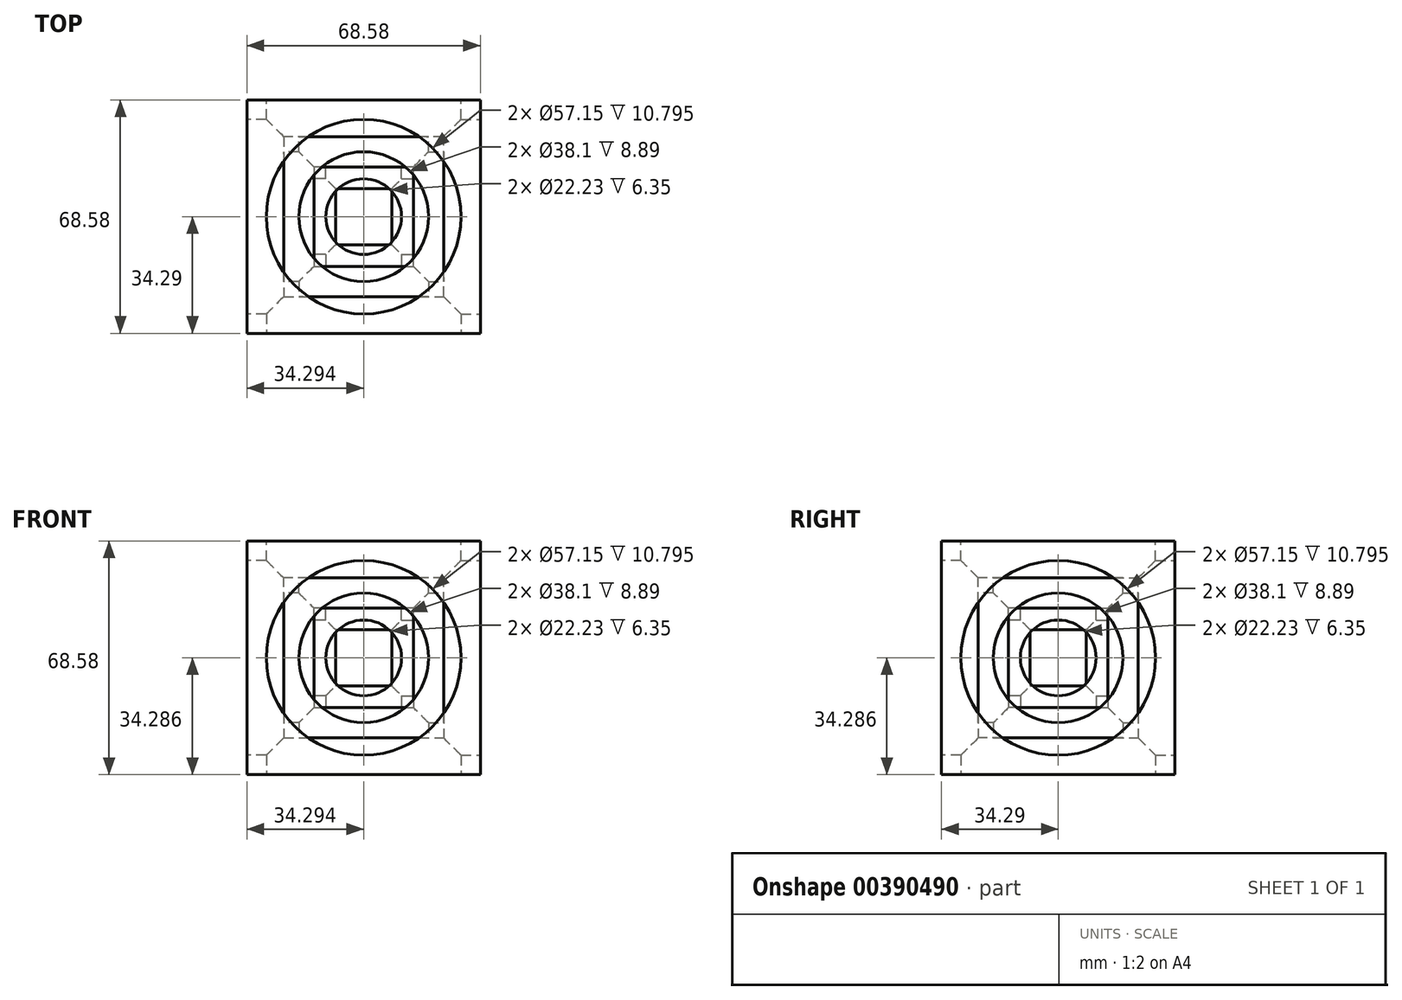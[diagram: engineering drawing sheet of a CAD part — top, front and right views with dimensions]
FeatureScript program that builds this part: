
annotation { "Feature Type Name" : "Feature", "Feature Type Description" : "" }
export const myFeature = defineFeature(function(context is Context, id is Id, definition is map)
    precondition{}
    {
        {
            var Q0;
            Q0=qCreatedBy(makeId("Front.planeOp"),FACE);
            var sketch = newSketch(context, id + "F0", { "sketchPlane" : qUnion([Q0])});
            skLineSegment(sketch, "E0.bottom", {"start": v(-23.47, 31.89) * mm, "end": v(45.11, 31.89) * mm});
            skLineSegment(sketch, "E0.top", {"start": v(-23.47, -36.7) * mm, "end": v(45.11, -36.7) * mm});
            skLineSegment(sketch, "E0.left", {"start": v(-23.47, 31.89) * mm, "end": v(-23.47, -36.7) * mm});
            skLineSegment(sketch, "E0.right", {"start": v(45.11, 31.89) * mm, "end": v(45.11, -36.7) * mm});
            skSolve(sketch);
        }
        {
            var Q0;
            Q0=makeQuery(id+"F0.imprint","IMPRINT",FACE,{"disambiguationData":[TD([[makeQuery(id+"F0.imprint","IMPRINT",EDGE,{"derivedFrom":sQuery(id+"F0.wireOp",EDGE,"E0.bottom")}),-1.0]])]});
            extrude(context, id + "F1", {"entities" : qUnion([Q0]), "depth" : 68.58 * mm});
        }
        {
            var Q0;
            Q0=makeQuery(id+"F1.opExtrude","CAP_FACE",FACE,{"disambiguationData":[OSD([sQuery(id+"F0.wireOp",EDGE,"E0.bottom"),sQuery(id+"F0.wireOp",EDGE,"E0.top"),sQuery(id+"F0.wireOp",EDGE,"E0.left"),sQuery(id+"F0.wireOp",EDGE,"E0.right")])],"isStart":false});
            var sketch = newSketch(context, id + "F2", { "sketchPlane" : qUnion([Q0])});
            skCircle(sketch, "E1", {"center": v(10.82, -2.4) * mm, "radius": 28.58 * mm});
            skPoint(sketch, "E1.centerSnap0", {"position": v(10.82, 31.89) * mm});
            skPoint(sketch, "E1.centerSnap1", {"position": v(-23.47, -2.4) * mm});
            skSolve(sketch);
        }
        {
            var Q0;
            Q0=makeQuery(id+"F2.imprint","IMPRINT",FACE,{"disambiguationData":[TD([[makeQuery(id+"F2.imprint","IMPRINT",EDGE,{"derivedFrom":sQuery(id+"F2.wireOp",EDGE,"E1")}),1.0]])]});
            extrude(context, id + "F3", {"entities" : qUnion([Q0]), "operationType" : NewBodyOperationType.REMOVE, "depth" : -10.8 * mm});
        }
        {
            var Q0;
            Q0=makeQuery(id+"F1.opExtrude","SWEPT_FACE",FACE,{"disambiguationData":[OSD([sQuery(id+"F0.wireOp",EDGE,"E0.right")])]});
            var sketch = newSketch(context, id + "F4", { "sketchPlane" : qUnion([Q0])});
            skCircle(sketch, "E2", {"center": v(-34.3, -2.4) * mm, "radius": 28.58 * mm});
            skPoint(sketch, "E2.centerSnap0", {"position": v(-68.58, -2.4) * mm});
            skPoint(sketch, "E2.centerSnap1", {"position": v(-34.3, 31.89) * mm});
            skSolve(sketch);
        }
        {
            var Q0;
            Q0=makeQuery(id+"F4.imprint","IMPRINT",FACE,{"disambiguationData":[TD([[makeQuery(id+"F4.imprint","IMPRINT",EDGE,{"derivedFrom":sQuery(id+"F4.wireOp",EDGE,"E2")}),1.0]])]});
            extrude(context, id + "F5", {"entities" : qUnion([Q0]), "operationType" : NewBodyOperationType.REMOVE, "oppositeDirection" : true, "depth" : 10.8 * mm});
        }
        {
            var Q0;
            Q0=makeQuery(id+"F1.opExtrude","CAP_FACE",FACE,{"disambiguationData":[OSD([sQuery(id+"F0.wireOp",EDGE,"E0.bottom"),sQuery(id+"F0.wireOp",EDGE,"E0.top"),sQuery(id+"F0.wireOp",EDGE,"E0.left"),sQuery(id+"F0.wireOp",EDGE,"E0.right")])],"isStart":true});
            var sketch = newSketch(context, id + "F6", { "sketchPlane" : qUnion([Q0])});
            skCircle(sketch, "E3", {"center": v(-10.82, -2.4) * mm, "radius": 28.58 * mm});
            skPoint(sketch, "E3.centerSnap0", {"position": v(-45.11, -2.4) * mm});
            skPoint(sketch, "E3.centerSnap1", {"position": v(-10.82, 31.89) * mm});
            skSolve(sketch);
        }
        {
            var Q0;
            Q0=makeQuery(id+"F6.imprint","IMPRINT",FACE,{"disambiguationData":[TD([[makeQuery(id+"F6.imprint","IMPRINT",EDGE,{"derivedFrom":sQuery(id+"F6.wireOp",EDGE,"E3")}),1.0]])]});
            extrude(context, id + "F7", {"entities" : qUnion([Q0]), "operationType" : NewBodyOperationType.REMOVE, "oppositeDirection" : true, "depth" : 10.8 * mm});
        }
        {
            var Q0;
            Q0=makeQuery(id+"F1.opExtrude","SWEPT_FACE",FACE,{"disambiguationData":[OSD([sQuery(id+"F0.wireOp",EDGE,"E0.left")])]});
            var sketch = newSketch(context, id + "F8", { "sketchPlane" : qUnion([Q0])});
            skCircle(sketch, "E4", {"center": v(34.3, -2.4) * mm, "radius": 28.58 * mm});
            skPoint(sketch, "E4.centerSnap0", {"position": v(68.58, -2.4) * mm});
            skPoint(sketch, "E4.centerSnap1", {"position": v(34.3, 31.89) * mm});
            skSolve(sketch);
        }
        {
            var Q0;
            Q0=makeQuery(id+"F8.imprint","IMPRINT",FACE,{"disambiguationData":[TD([[makeQuery(id+"F8.imprint","IMPRINT",EDGE,{"derivedFrom":sQuery(id+"F8.wireOp",EDGE,"E4")}),1.0]])]});
            extrude(context, id + "F9", {"entities" : qUnion([Q0]), "operationType" : NewBodyOperationType.REMOVE, "oppositeDirection" : true, "depth" : 10.8 * mm});
        }
        {
            var Q0;
            Q0=makeQuery(id+"F1.opExtrude","SWEPT_FACE",FACE,{"disambiguationData":[OSD([sQuery(id+"F0.wireOp",EDGE,"E0.bottom")])]});
            var sketch = newSketch(context, id + "F10", { "sketchPlane" : qUnion([Q0])});
            skCircle(sketch, "E5", {"center": v(10.82, -34.3) * mm, "radius": 28.58 * mm});
            skPoint(sketch, "E5.centerSnap0", {"position": v(10.82, -68.58) * mm});
            skPoint(sketch, "E5.centerSnap1", {"position": v(-23.47, -34.3) * mm});
            skSolve(sketch);
        }
        {
            var Q0;
            Q0=makeQuery(id+"F10.imprint","IMPRINT",FACE,{"disambiguationData":[TD([[makeQuery(id+"F10.imprint","IMPRINT",EDGE,{"derivedFrom":sQuery(id+"F10.wireOp",EDGE,"E5")}),1.0]])]});
            extrude(context, id + "F11", {"entities" : qUnion([Q0]), "operationType" : NewBodyOperationType.REMOVE, "oppositeDirection" : true, "depth" : 10.8 * mm});
        }
        {
            var Q0;
            Q0=makeQuery(id+"F1.opExtrude","SWEPT_FACE",FACE,{"disambiguationData":[OSD([sQuery(id+"F0.wireOp",EDGE,"E0.top")])]});
            var sketch = newSketch(context, id + "F12", { "sketchPlane" : qUnion([Q0])});
            skCircle(sketch, "E6", {"center": v(10.82, 34.3) * mm, "radius": 28.58 * mm});
            skPoint(sketch, "E6.centerSnap0", {"position": v(10.82, 68.58) * mm});
            skPoint(sketch, "E6.centerSnap1", {"position": v(-23.47, 34.3) * mm});
            skSolve(sketch);
        }
        {
            var Q0;
            Q0=makeQuery(id+"F12.imprint","IMPRINT",FACE,{"disambiguationData":[TD([[makeQuery(id+"F12.imprint","IMPRINT",EDGE,{"derivedFrom":sQuery(id+"F12.wireOp",EDGE,"E6")}),1.0]])]});
            extrude(context, id + "F13", {"entities" : qUnion([Q0]), "operationType" : NewBodyOperationType.REMOVE, "oppositeDirection" : true, "depth" : 10.8 * mm});
        }
        {
            var Q0;
            Q0=makeQuery(id+"F3.boolean.opBoolean","COPY",FACE,{"derivedFrom":makeQuery(id+"F3.opExtrude","CAP_FACE",FACE,{"disambiguationData":[OSD([sQuery(id+"F2.wireOp",EDGE,"E1")])],"isStart":false})});
            var sketch = newSketch(context, id + "F14", { "sketchPlane" : qUnion([Q0])});
            skPoint(sketch, "E7.centerSnap0", {"position": v(10.82, 21.1) * mm});
            skCircle(sketch, "E8", {"center": v(10.82, -2.4) * mm, "radius": 19.05 * mm});
            skSolve(sketch);
        }
        {
            var Q0;
            Q0=makeQuery(id+"F14.imprint","IMPRINT",FACE,{"disambiguationData":[TD([[makeQuery(id+"F14.imprint","IMPRINT",EDGE,{"derivedFrom":sQuery(id+"F14.wireOp",EDGE,"E8")}),1.0]])]});
            extrude(context, id + "F15", {"entities" : qUnion([Q0]), "operationType" : NewBodyOperationType.REMOVE, "oppositeDirection" : true, "depth" : 8.9 * mm});
        }
        {
            var Q0;
            Q0=makeQuery(id+"F5.boolean.opBoolean","COPY",FACE,{"derivedFrom":makeQuery(id+"F5.opExtrude","CAP_FACE",FACE,{"disambiguationData":[OSD([sQuery(id+"F4.wireOp",EDGE,"E2")])],"isStart":false})});
            var sketch = newSketch(context, id + "F16", { "sketchPlane" : qUnion([Q0])});
            skCircle(sketch, "E9", {"center": v(-34.3, -2.4) * mm, "radius": 19.05 * mm});
            skSolve(sketch);
        }
        {
            var Q0;
            Q0=makeQuery(id+"F16.imprint","IMPRINT",FACE,{"disambiguationData":[TD([[makeQuery(id+"F16.imprint","IMPRINT",EDGE,{"derivedFrom":sQuery(id+"F16.wireOp",EDGE,"E9")}),1.0]])]});
            extrude(context, id + "F17", {"entities" : qUnion([Q0]), "operationType" : NewBodyOperationType.REMOVE, "oppositeDirection" : true, "depth" : 8.9 * mm});
        }
        {
            var Q0;
            Q0=makeQuery(id+"F7.boolean.opBoolean","COPY",FACE,{"derivedFrom":makeQuery(id+"F7.opExtrude","CAP_FACE",FACE,{"disambiguationData":[OSD([sQuery(id+"F6.wireOp",EDGE,"E3")])],"isStart":false})});
            var sketch = newSketch(context, id + "F18", { "sketchPlane" : qUnion([Q0])});
            skCircle(sketch, "E10", {"center": v(-10.82, -2.4) * mm, "radius": 19.05 * mm});
            skSolve(sketch);
        }
        {
            var Q0;
            Q0=makeQuery(id+"F18.imprint","IMPRINT",FACE,{"disambiguationData":[TD([[makeQuery(id+"F18.imprint","IMPRINT",EDGE,{"derivedFrom":sQuery(id+"F18.wireOp",EDGE,"E10")}),1.0]])]});
            extrude(context, id + "F19", {"entities" : qUnion([Q0]), "operationType" : NewBodyOperationType.REMOVE, "oppositeDirection" : true, "depth" : 8.9 * mm});
        }
        {
            var Q0;
            Q0=makeQuery(id+"F9.boolean.opBoolean","COPY",FACE,{"derivedFrom":makeQuery(id+"F9.opExtrude","CAP_FACE",FACE,{"disambiguationData":[OSD([sQuery(id+"F8.wireOp",EDGE,"E4")])],"isStart":false})});
            var sketch = newSketch(context, id + "F20", { "sketchPlane" : qUnion([Q0])});
            skCircle(sketch, "E11", {"center": v(34.3, -2.4) * mm, "radius": 19.05 * mm});
            skSolve(sketch);
        }
        {
            var Q0;
            Q0=makeQuery(id+"F20.imprint","IMPRINT",FACE,{"disambiguationData":[TD([[makeQuery(id+"F20.imprint","IMPRINT",EDGE,{"derivedFrom":sQuery(id+"F20.wireOp",EDGE,"E11")}),1.0]])]});
            extrude(context, id + "F21", {"entities" : qUnion([Q0]), "operationType" : NewBodyOperationType.REMOVE, "oppositeDirection" : true, "depth" : 8.9 * mm});
        }
        {
            var Q0;
            Q0=makeQuery(id+"F11.boolean.opBoolean","COPY",FACE,{"derivedFrom":makeQuery(id+"F11.opExtrude","CAP_FACE",FACE,{"disambiguationData":[OSD([sQuery(id+"F10.wireOp",EDGE,"E5")])],"isStart":false})});
            var sketch = newSketch(context, id + "F22", { "sketchPlane" : qUnion([Q0])});
            skCircle(sketch, "E12", {"center": v(10.82, -34.3) * mm, "radius": 19.05 * mm});
            skSolve(sketch);
        }
        {
            var Q0;
            Q0=makeQuery(id+"F22.imprint","IMPRINT",FACE,{"disambiguationData":[TD([[makeQuery(id+"F22.imprint","IMPRINT",EDGE,{"derivedFrom":sQuery(id+"F22.wireOp",EDGE,"E12")}),1.0]])]});
            extrude(context, id + "F23", {"entities" : qUnion([Q0]), "operationType" : NewBodyOperationType.REMOVE, "oppositeDirection" : true, "depth" : 8.9 * mm});
        }
        {
            var Q0;
            Q0=makeQuery(id+"F13.boolean.opBoolean","COPY",FACE,{"derivedFrom":makeQuery(id+"F13.opExtrude","CAP_FACE",FACE,{"disambiguationData":[OSD([sQuery(id+"F12.wireOp",EDGE,"E6")])],"isStart":false})});
            var sketch = newSketch(context, id + "F24", { "sketchPlane" : qUnion([Q0])});
            skCircle(sketch, "E13", {"center": v(10.82, 34.3) * mm, "radius": 19.05 * mm});
            skSolve(sketch);
        }
        {
            var Q0;
            Q0=makeQuery(id+"F24.imprint","IMPRINT",FACE,{"disambiguationData":[TD([[makeQuery(id+"F24.imprint","IMPRINT",EDGE,{"derivedFrom":sQuery(id+"F24.wireOp",EDGE,"E13")}),1.0]])]});
            extrude(context, id + "F25", {"entities" : qUnion([Q0]), "operationType" : NewBodyOperationType.REMOVE, "oppositeDirection" : true, "depth" : 8.9 * mm});
        }
        {
            var Q0;
            Q0=makeQuery(id+"F17.boolean.opBoolean","COPY",FACE,{"derivedFrom":makeQuery(id+"F17.opExtrude","CAP_FACE",FACE,{"disambiguationData":[OSD([sQuery(id+"F16.wireOp",EDGE,"E9")])],"isStart":false})});
            var sketch = newSketch(context, id + "F26", { "sketchPlane" : qUnion([Q0])});
            skCircle(sketch, "E14", {"center": v(-34.3, -2.4) * mm, "radius": 11.11 * mm});
            skSolve(sketch);
        }
        {
            var Q0;
            Q0=makeQuery(id+"F26.imprint","IMPRINT",FACE,{"disambiguationData":[TD([[makeQuery(id+"F26.imprint","IMPRINT",EDGE,{"derivedFrom":sQuery(id+"F26.wireOp",EDGE,"E14")}),1.0]])]});
            extrude(context, id + "F27", {"entities" : qUnion([Q0]), "operationType" : NewBodyOperationType.REMOVE, "oppositeDirection" : true, "depth" : 6.35 * mm});
        }
        {
            var Q0;
            Q0=makeQuery(id+"F23.boolean.opBoolean","COPY",FACE,{"derivedFrom":makeQuery(id+"F23.opExtrude","CAP_FACE",FACE,{"disambiguationData":[OSD([sQuery(id+"F22.wireOp",EDGE,"E12")])],"isStart":false})});
            var sketch = newSketch(context, id + "F28", { "sketchPlane" : qUnion([Q0])});
            skCircle(sketch, "E15", {"center": v(10.82, -34.3) * mm, "radius": 11.11 * mm});
            skSolve(sketch);
        }
        {
            var Q0;
            Q0=makeQuery(id+"F28.imprint","IMPRINT",FACE,{"disambiguationData":[TD([[makeQuery(id+"F28.imprint","IMPRINT",EDGE,{"derivedFrom":sQuery(id+"F28.wireOp",EDGE,"E15")}),1.0]])]});
            extrude(context, id + "F29", {"entities" : qUnion([Q0]), "operationType" : NewBodyOperationType.REMOVE, "oppositeDirection" : true, "depth" : 6.35 * mm});
        }
        {
            var Q0;
            Q0=makeQuery(id+"F15.boolean.opBoolean","COPY",FACE,{"derivedFrom":makeQuery(id+"F15.opExtrude","CAP_FACE",FACE,{"disambiguationData":[OSD([sQuery(id+"F14.wireOp",EDGE,"E8")])],"isStart":false})});
            var sketch = newSketch(context, id + "F30", { "sketchPlane" : qUnion([Q0])});
            skCircle(sketch, "E16", {"center": v(10.82, -2.4) * mm, "radius": 11.11 * mm});
            skSolve(sketch);
        }
        {
            var Q0;
            Q0=makeQuery(id+"F30.imprint","IMPRINT",FACE,{"disambiguationData":[TD([[makeQuery(id+"F30.imprint","IMPRINT",EDGE,{"derivedFrom":sQuery(id+"F30.wireOp",EDGE,"E16")}),1.0]])]});
            extrude(context, id + "F31", {"entities" : qUnion([Q0]), "operationType" : NewBodyOperationType.REMOVE, "oppositeDirection" : true, "depth" : 6.35 * mm});
        }
        {
            var Q0;
            Q0=makeQuery(id+"F19.boolean.opBoolean","COPY",FACE,{"derivedFrom":makeQuery(id+"F19.opExtrude","CAP_FACE",FACE,{"disambiguationData":[OSD([sQuery(id+"F18.wireOp",EDGE,"E10")])],"isStart":false})});
            var sketch = newSketch(context, id + "F32", { "sketchPlane" : qUnion([Q0])});
            skCircle(sketch, "E17", {"center": v(-10.82, -2.4) * mm, "radius": 11.11 * mm});
            skSolve(sketch);
        }
        {
            var Q0;
            Q0=makeQuery(id+"F32.imprint","IMPRINT",FACE,{"disambiguationData":[TD([[makeQuery(id+"F32.imprint","IMPRINT",EDGE,{"derivedFrom":sQuery(id+"F32.wireOp",EDGE,"E17")}),1.0]])]});
            extrude(context, id + "F33", {"entities" : qUnion([Q0]), "operationType" : NewBodyOperationType.REMOVE, "oppositeDirection" : true, "depth" : 6.35 * mm});
        }
        {
            var Q0;
            Q0=makeQuery(id+"F25.boolean.opBoolean","COPY",FACE,{"derivedFrom":makeQuery(id+"F25.opExtrude","CAP_FACE",FACE,{"disambiguationData":[OSD([sQuery(id+"F24.wireOp",EDGE,"E13")])],"isStart":false})});
            var sketch = newSketch(context, id + "F34", { "sketchPlane" : qUnion([Q0])});
            skCircle(sketch, "E18", {"center": v(10.82, 34.3) * mm, "radius": 11.11 * mm});
            skSolve(sketch);
        }
        {
            var Q0;
            Q0=makeQuery(id+"F34.imprint","IMPRINT",FACE,{"disambiguationData":[TD([[makeQuery(id+"F34.imprint","IMPRINT",EDGE,{"derivedFrom":sQuery(id+"F34.wireOp",EDGE,"E18")}),1.0]])]});
            extrude(context, id + "F35", {"entities" : qUnion([Q0]), "operationType" : NewBodyOperationType.REMOVE, "oppositeDirection" : true, "depth" : 6.35 * mm});
        }
        {
            var Q0;
            Q0=makeQuery(id+"F21.boolean.opBoolean","COPY",FACE,{"derivedFrom":makeQuery(id+"F21.opExtrude","CAP_FACE",FACE,{"disambiguationData":[OSD([sQuery(id+"F20.wireOp",EDGE,"E11")])],"isStart":false})});
            var sketch = newSketch(context, id + "F36", { "sketchPlane" : qUnion([Q0])});
            skCircle(sketch, "E19", {"center": v(34.3, -2.4) * mm, "radius": 11.11 * mm});
            skSolve(sketch);
        }
        {
            var Q0;
            Q0=makeQuery(id+"F36.imprint","IMPRINT",FACE,{"disambiguationData":[TD([[makeQuery(id+"F36.imprint","IMPRINT",EDGE,{"derivedFrom":sQuery(id+"F36.wireOp",EDGE,"E19")}),1.0]])]});
            extrude(context, id + "F37", {"entities" : qUnion([Q0]), "operationType" : NewBodyOperationType.REMOVE, "oppositeDirection" : true, "depth" : 6.35 * mm});
        }
    });
